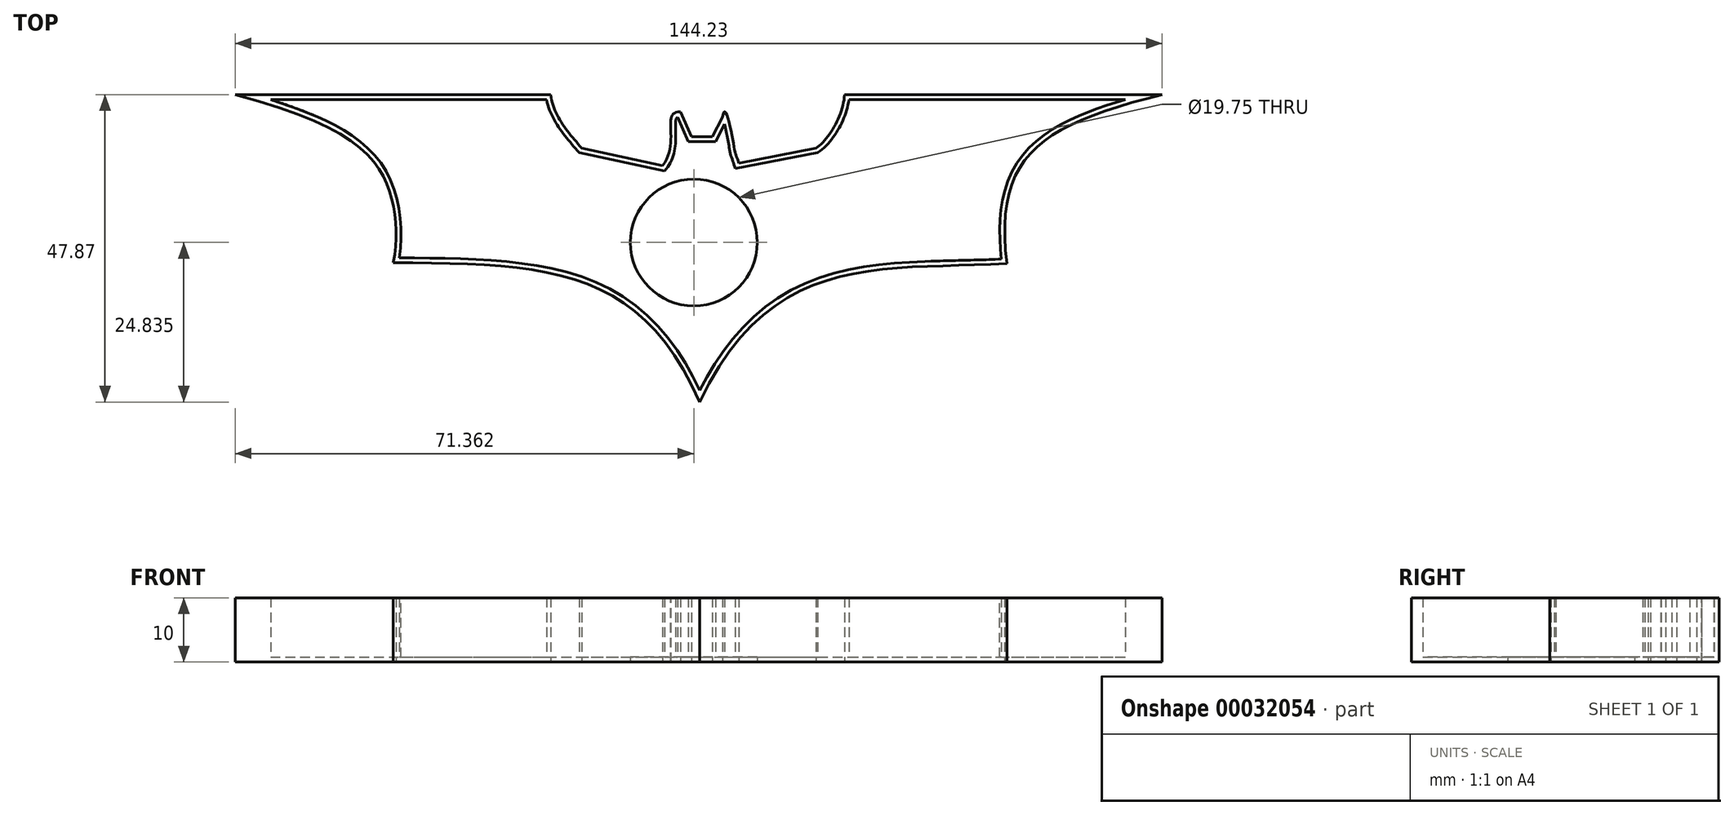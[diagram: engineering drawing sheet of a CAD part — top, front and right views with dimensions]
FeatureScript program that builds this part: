
annotation { "Feature Type Name" : "Feature", "Feature Type Description" : "" }
export const myFeature = defineFeature(function(context is Context, id is Id, definition is map)
    precondition{}
    {
        {
            var Q0;
            Q0=qCreatedBy(makeId("Top.planeOp"),FACE);
            var sketch = newSketch(context, id + "F0", { "sketchPlane" : qUnion([Q0])});
            skLineSegment(sketch, "E0", {"start": v(-69.3, 29.8) * mm, "end": v(-20.24, 29.8) * mm});
            skLineSegment(sketch, "E1", {"start": v(-15.4, 21.5) * mm, "end": v(-2.8, 18.8) * mm});
            skLineSegment(sketch, "E2", {"start": v(1.66, 23.25) * mm, "end": v(0, 27.13) * mm});
            skLineSegment(sketch, "E3", {"start": v(1.66, 23.25) * mm, "end": v(4.96, 23.25) * mm});
            skLineSegment(sketch, "E4", {"start": v(4.96, 23.25) * mm, "end": v(6.5, 26.35) * mm});
            skLineSegment(sketch, "E5", {"start": v(9.03, 19.18) * mm, "end": v(21.04, 21.5) * mm});
            skLineSegment(sketch, "E6", {"start": v(25.5, 29.84) * mm, "end": v(74.92, 29.84) * mm});
            skFitSpline(sketch, "E7", {"points": [v(-69.3, 29.8) * mm, v(-45.22, 14.53) * mm, v(-44.72, 3.68) * mm], "startDerivative": vector(87.78, -22.6) * mm, "endDerivative": vector(-5.65, -28.81) * mm});
            skFitSpline(sketch, "E8", {"points": [v(-44.72, 3.68) * mm, v(2.94, -18.03) * mm], "startDerivative": vector(70.72, -0.5) * mm, "endDerivative": vector(27.47, -63.6) * mm});
            skFitSpline(sketch, "E9", {"points": [v(2.94, -18.03) * mm, v(50.76, 3.5) * mm], "startDerivative": vector(33.58, 70.72) * mm, "endDerivative": vector(58.5, 3.05) * mm});
            skFitSpline(sketch, "E10", {"points": [v(50.76, 3.5) * mm, v(74.92, 29.84) * mm], "startDerivative": vector(-6.1, 50.37) * mm, "endDerivative": vector(57.23, 14.4) * mm});
            skFitSpline(sketch, "E11", {"points": [v(-20.24, 29.8) * mm, v(-15.4, 21.5) * mm], "startDerivative": vector(1.35, -9.67) * mm, "endDerivative": vector(6.57, -7.55) * mm});
            skFitSpline(sketch, "E12", {"points": [v(-2.8, 18.8) * mm, v(0, 27.13) * mm], "startDerivative": vector(8.39, 11.11) * mm, "endDerivative": vector(9.5, -0.86) * mm});
            skFitSpline(sketch, "E13", {"points": [v(6.5, 26.35) * mm, v(8.38, 21.32) * mm, v(9.03, 19.18) * mm], "startDerivative": vector(2.46, 15.28) * mm, "endDerivative": vector(4.99, -16.32) * mm});
            skFitSpline(sketch, "E14", {"points": [v(21.04, 21.5) * mm, v(25.5, 29.84) * mm], "startDerivative": vector(6.22, 3.99) * mm, "endDerivative": vector(0.54, 9.31) * mm});
            skSolve(sketch);
        }
        {
            var Q0;
            Q0=makeQuery(id+"F0.imprint","IMPRINT",FACE,{"disambiguationData":[TD([[makeQuery(id+"F0.imprint","IMPRINT",EDGE,{"derivedFrom":sQuery(id+"F0.wireOp",EDGE,"E0")}),-1.0]])]});
            extrude(context, id + "F1", {"entities" : qUnion([Q0]), "depth" : 10 * mm});
        }
        {
            var Q0;
            Q0=makeQuery(id+"F1.opExtrude","CAP_FACE",FACE,{"disambiguationData":[OSD([sQuery(id+"F0.wireOp",EDGE,"E0"),sQuery(id+"F0.wireOp",EDGE,"E1"),sQuery(id+"F0.wireOp",EDGE,"E2"),sQuery(id+"F0.wireOp",EDGE,"E3"),sQuery(id+"F0.wireOp",EDGE,"E4"),sQuery(id+"F0.wireOp",EDGE,"E5"),sQuery(id+"F0.wireOp",EDGE,"E6"),sQuery(id+"F0.wireOp",EDGE,"E7"),sQuery(id+"F0.wireOp",EDGE,"E8"),sQuery(id+"F0.wireOp",EDGE,"E9"),sQuery(id+"F0.wireOp",EDGE,"E10"),sQuery(id+"F0.wireOp",EDGE,"E11"),sQuery(id+"F0.wireOp",EDGE,"E12"),sQuery(id+"F0.wireOp",EDGE,"E13"),sQuery(id+"F0.wireOp",EDGE,"E14")])],"isStart":false});
            shell(context, id + "F2", {"entities" : qUnion([Q0]), "thickness" : 0.76 * mm});
        }
        {
            var Q0;
            Q0=qCreatedBy(makeId("Top.planeOp"),FACE);
            var sketch = newSketch(context, id + "F3", { "sketchPlane" : qUnion([Q0])});
            skCircle(sketch, "E15", {"center": v(2.05, 6.8) * mm, "radius": 9.87 * mm});
            skSolve(sketch);
        }
        {
            var Q0;
            Q0 = qSketchRegion(id + "F3", true);
            extrude(context, id + "F4", {"entities" : qUnion([Q0]), "operationType" : NewBodyOperationType.REMOVE, "depth" : 25.4 * mm});
        }
    });
